# Revit family: CADS_AIRFLOWdev_Switches
name_source: partatom
category: Electrical Fixtures
revit_build: Autodesk Revit 2015 (Build: 20160512_1515(x64)
units: mm (PartAtom-declared; Revit-internal decimal feet)

## types (1)
- Isolation Switch
    AssetType = Fixed
    Body = CADS_Airflow_Switch_Body
    CADS_Index = 0
    CEApproval = Yes
    Color = White
    Constituents = White
    Default Elevation = 1219 mm
    Description = Isolation Switch
    Double_Switch = No
    Double_Switch_Type = Empty_Switch
    DurationUnit = Years
    Exclusions = Incorrect Use / Incorrect Installation / Installed by a non-accredited electrician. Customer abuse.
    Finish = White
    GlobalTradeItemNumber = 5019009319568
    GrossWeight = 0.25 kg
    HasLock = No
    HasProtectiveEarth = No
    IP_Code = IP20
    ISO140001 = Yes
    ISO90001 = Yes
    IsExtendedWarranty = No
    IsIlluminated = No
    L = 87 mm  [stored 0.285433 ft]
    Legend = YES
    Light = CADS_Airflow_Light_Red
    Manufacturer = Airflow Developments Ltd
    ManufacturerAddress = Aidelle House
Lancaster Road
Cressex Business Park
High Wycombe
Bucks
HP123QP
    ManufacturerTelephone = 01494 525252
    ManufacturerWebsite = www.airflow.com
    Material = Plastic
    ModelLabel = Isolation Switch
    ModelReference = 90000537
    NBSCode = 90-60-25/325 Light switches;
    NominalFrequencyRange = 50/60
    NominalHeight = 86 mm  [stored 0.282152 ft]
    NominalLength = 16 mm  [stored 0.0524934 ft]
    NominalWidth = 86 mm  [stored 0.282152 ft]
    NumberOfGangs = 1
    NumberOfPoles = 1
    OppLight = CADS_Airflow_Light_Red
    PointOfContact = Airflow Developments Ltd
    ProductionYear = 2017
    Quantity = 1
    RatedCurrent = 0 A
    RatedVoltage = 230 V
    ReplacementCost = 25.536
    ServiceLifeDuration = 10
    ServiceLifeType = ExpectedServiceLife
    SetPoint = YES
    Shape = Rectangular
    ShippingWeight = 0.35 kg
    Single_Double = 0 mm  [stored 0 ft]
    Single_Switch = Yes
    Single_Switch_Type = Single_Switch
    Size = 86x16x86
    SupplyPhase = 1
    SwitchFunction = Rocker
    Uniclass2015 = Pr_75_51_17_50
    W = 87 mm  [stored 0.285433 ft]
    WarrantyContent = See Airflow Developments Ltd warranty terms.
    WarrantyGuarantor = Airflow Developments Ltd

note: [stored X ft] marks values corroborated as IEEE doubles in the binary element streams (Revit-internal decimal feet)

## geometry (parser evidence)
native form markers: Blend x4, Sweep x35
no freeform markers — native parametric forms only
